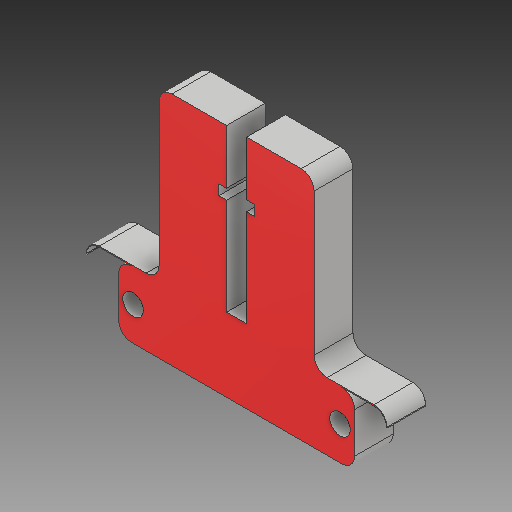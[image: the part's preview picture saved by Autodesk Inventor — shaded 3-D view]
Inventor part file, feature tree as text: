
AUTODESK INVENTOR PART (.ipt)
format: ipt  version: 2017 (Build 210142000, 142)  size: 185,344 bytes
history: native  units: mm
features: sketch x6, other x3
ambient origin geometry x8: Origin, YZ Plane, XZ Plane, XY Plane, X Axis, Y Axis, Z Axis, Center Point
bodies: Solid1 (feature_tree)
feature tree (9):
  other  "Hotend Slide Part 1.ipt"
  other  "Solid1::Hotend Slide Part 1.ipt"
  other  "TaggingFeature1"
  sketch  "Sketch1"  dims[d0=10.0mm]
  sketch  "Sketch2"
  sketch  "Sketch3"
  sketch  "Sketch4"
  sketch  "Sketch5"
  sketch  "Sketch6"
